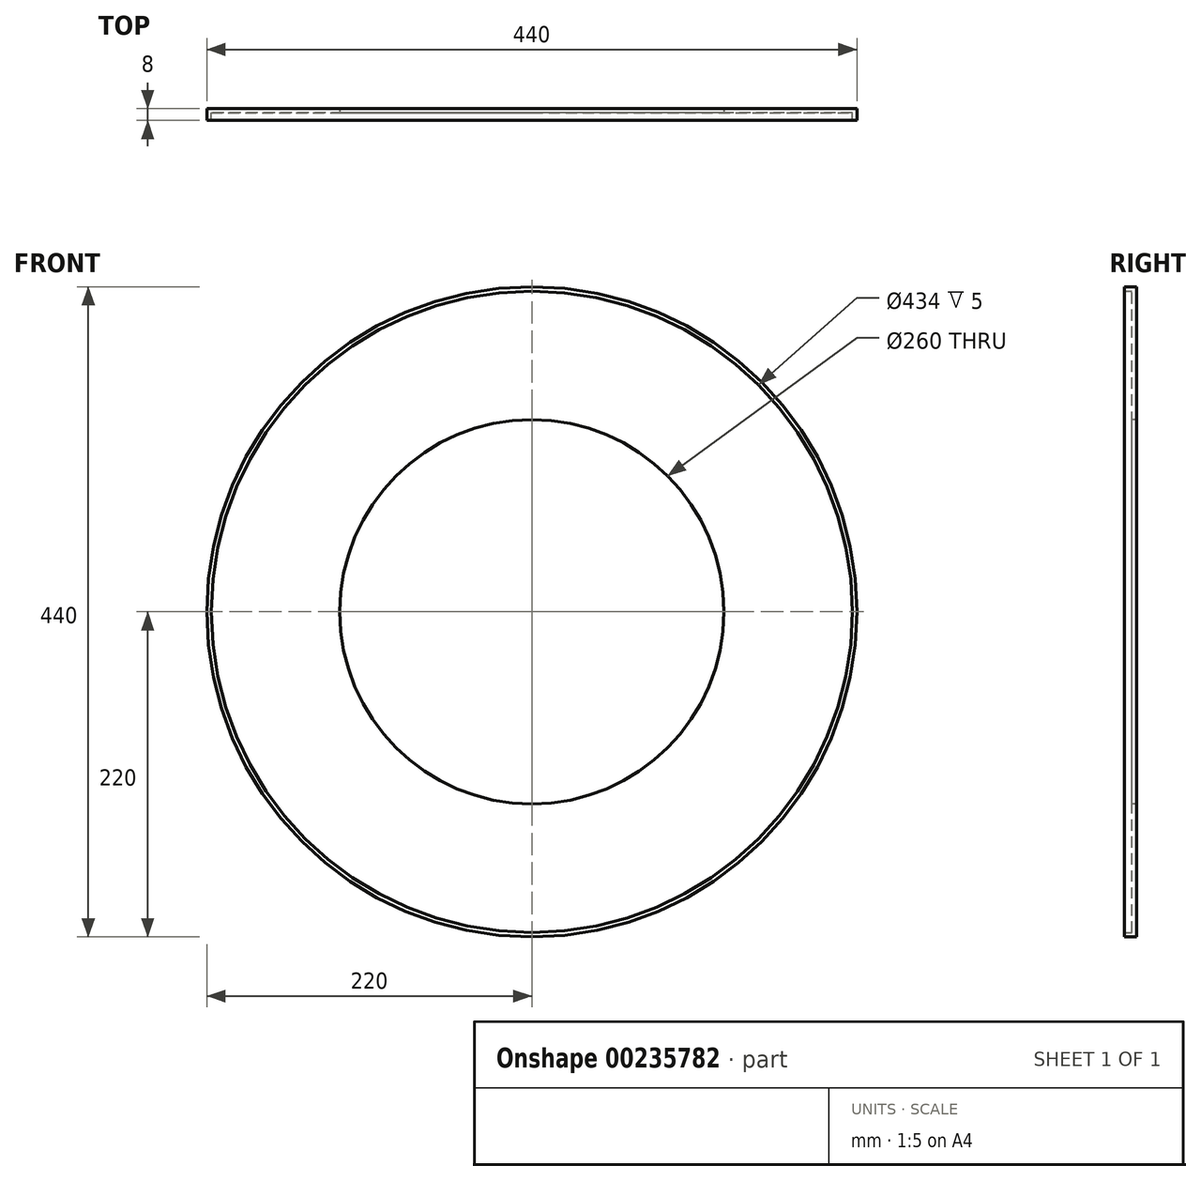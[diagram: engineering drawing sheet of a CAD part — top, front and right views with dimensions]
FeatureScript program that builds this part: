
annotation { "Feature Type Name" : "Feature", "Feature Type Description" : "" }
export const myFeature = defineFeature(function(context is Context, id is Id, definition is map)
    precondition{}
    {
        {
            var Q0;
            Q0=qCreatedBy(makeId("Front.planeOp"),FACE);
            var sketch = newSketch(context, id + "F0", { "sketchPlane" : qUnion([Q0])});
            skCircle(sketch, "E0", {"center": v(0, 0) * mm, "radius": 220 * mm});
            skSolve(sketch);
        }
        {
            var Q0;
            Q0=makeQuery(id+"F0.imprint","IMPRINT",FACE,{"disambiguationData":[TD([[makeQuery(id+"F0.imprint","IMPRINT",EDGE,{"derivedFrom":sQuery(id+"F0.wireOp",EDGE,"E0")}),1.0]])]});
            extrude(context, id + "F1", {"entities" : qUnion([Q0]), "depth" : 8 * mm});
        }
        {
            var Q0;
            Q0=makeQuery(id+"F1.opExtrude","CAP_FACE",FACE,{"disambiguationData":[OSD([sQuery(id+"F0.wireOp",EDGE,"E0")])],"isStart":false});
            shell(context, id + "F2", {"entities" : qUnion([Q0]), "thickness" : 3 * mm});
        }
        {
            var Q0;
            Q0=makeQuery(id+"F1.opExtrude","CAP_FACE",FACE,{"disambiguationData":[OSD([sQuery(id+"F0.wireOp",EDGE,"E0")])],"isStart":false});
            var sketch = newSketch(context, id + "F3", { "sketchPlane" : qUnion([Q0])});
            skCircle(sketch, "E1", {"center": v(0, 0) * mm, "radius": 130 * mm});
            skSolve(sketch);
        }
        {
            var Q0;
            Q0=makeQuery(id+"F3.imprint","IMPRINT",FACE,{"disambiguationData":[TD([[makeQuery(id+"F3.imprint","IMPRINT",EDGE,{"derivedFrom":sQuery(id+"F3.wireOp",EDGE,"E1")}),1.0]])]});
            extrude(context, id + "F4", {"entities" : qUnion([Q0]), "operationType" : NewBodyOperationType.REMOVE, "endBound" : BoundingType.THROUGH_ALL, "oppositeDirection" : true, "depth" : 25 * mm});
        }
    });
